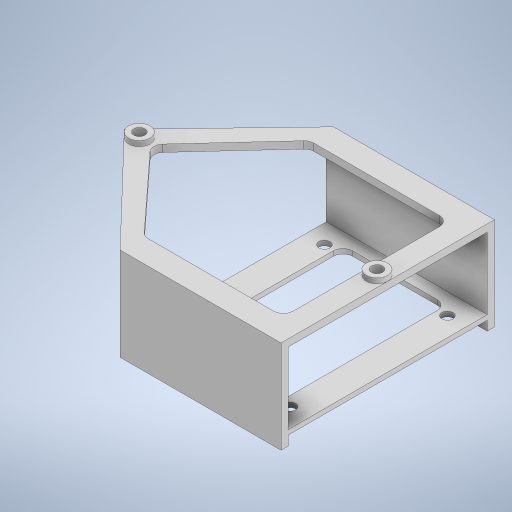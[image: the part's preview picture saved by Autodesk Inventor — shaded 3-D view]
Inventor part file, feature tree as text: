
AUTODESK INVENTOR PART (.ipt)
format: ipt  version: 2023 (Build 270158030, 158C)  size: 339,456 bytes
history: native  units: in
note: dims shown in document units (in); Inventor stores cm internally (conversion verified against a paired STEP export)
features: extrude x6, sketch x4, projected_geometry x2, fillet x1
ambient origin geometry x8: Origin, YZ Plane, XZ Plane, XY Plane, X Axis, Y Axis, Z Axis, Center Point
bodies: Solid1 (feature_tree)
feature tree (13):
  sketch  "Sketch1"  dims[d0=3.2874in d1=0.1181in]
  extrude  "Extrusion1"  Depth=0.1181in
  extrude  "Extrusion2"  Depth=0.1969in
  extrude  "Extrusion3"  Depth=0.4724in
  sketch  "Sketch3"  dims[d5=0.1969in d6=0.4724in]
  extrude  "Extrusion4"  Depth=2.6575in
  extrude  "Extrusion5"  Depth=0.1575in
  extrude  "Extrusion6"  Depth=0.1575in
  fillet  "Fillet1"  Radius=0.0787in
  sketch  "Sketch2"  dims[d2=0.1181in d4=0.1969in]
  projected_geometry  "Projected Loop1"
  projected_geometry  "Projected Loop2"
  sketch  "Sketch4"  dims[d7=0.4724in d8=2.6575in d9=1.3287in d10=1.6437in d11=0.0787in d12=0.0in d13=1.2598in d14=0.1575in d15=0.0in d16=0.0in d18=0.2756in d19=0.2756in d20=4.3504in d21=3.563in d22=0.1181in d23=0.0in d24=0.3543in d27=0.185in d31=0.0846in d32=0.0in d33=0.1181in d34=0.0in d35=0.185in d36=0.313in d37=0.3445in d38=0.313in d39=0.3445in d40=0.1181in d41=0.0in d42=0.3543in d43=3.9252in d44=0.1772in d45=0.1575in]
